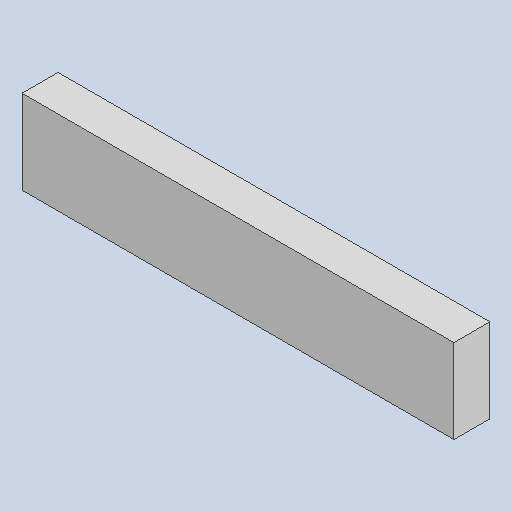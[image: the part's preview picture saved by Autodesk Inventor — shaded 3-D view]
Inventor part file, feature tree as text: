
AUTODESK INVENTOR PART (.ipt)
format: ipt  version: 2025 (Build 290162000, 162)  size: 80,896 bytes
history: native  units: in
note: dims shown in document units (in); Inventor stores cm internally (conversion verified against a paired STEP export)
features: other x3, sketch x1
ambient origin geometry x8: Origin, YZ Plane, XZ Plane, XY Plane, X Axis, Y Axis, Z Axis, Center Point
bodies: Solid1 (feature_tree)
feature tree (4):
  other  "back-side.ipt"
  other  "Solid1::back-side.ipt"
  other  "TaggingFeature1"
  sketch  "Sketch1"  dims[d0=0.3937in]
